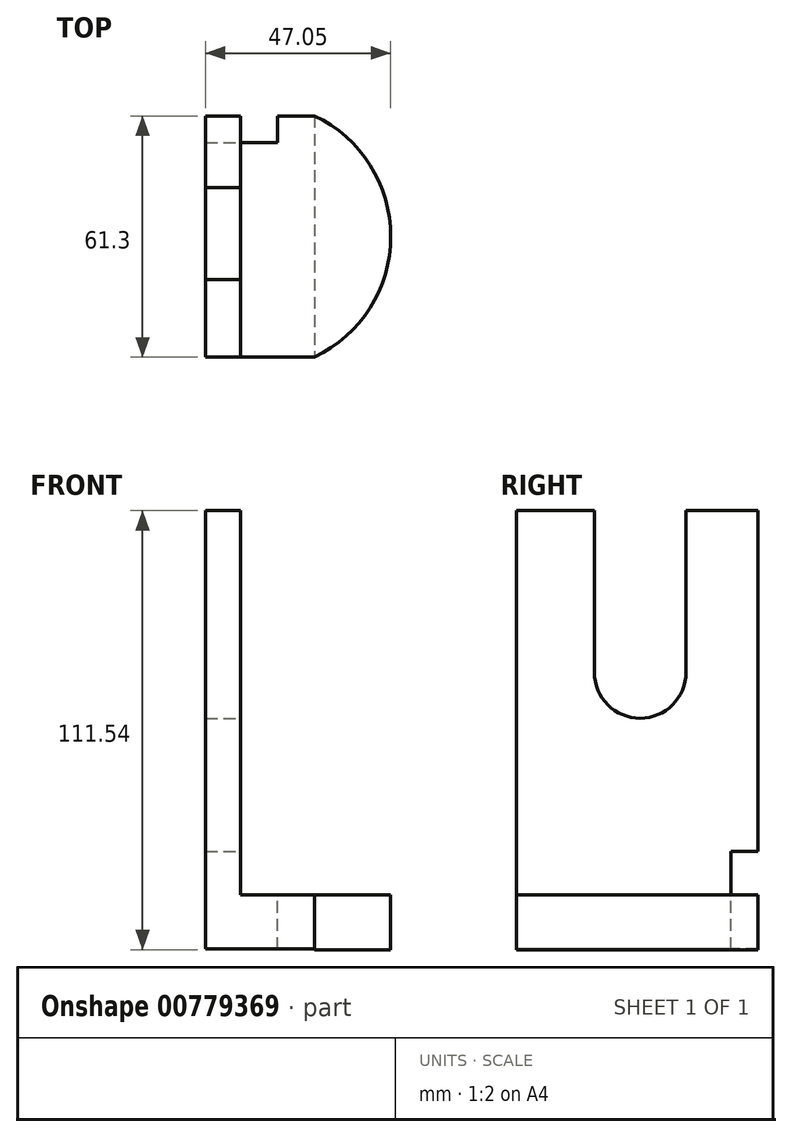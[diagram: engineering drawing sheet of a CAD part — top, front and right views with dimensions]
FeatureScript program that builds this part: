
annotation { "Feature Type Name" : "Feature", "Feature Type Description" : "" }
export const myFeature = defineFeature(function(context is Context, id is Id, definition is map)
    precondition{}
    {
        {
            var Q0;
            Q0=qCreatedBy(makeId("Right.planeOp"),FACE);
            var sketch = newSketch(context, id + "F0", { "sketchPlane" : qUnion([Q0])});
            skLineSegment(sketch, "E0.bottom", {"start": v(30.65, 55.7) * mm, "end": v(-30.65, 55.7) * mm});
            skLineSegment(sketch, "E0.top", {"start": v(30.65, -55.7) * mm, "end": v(-30.65, -55.7) * mm});
            skLineSegment(sketch, "E0.left", {"start": v(30.65, 55.7) * mm, "end": v(30.65, -55.7) * mm});
            skLineSegment(sketch, "E0.right", {"start": v(-30.65, 55.7) * mm, "end": v(-30.65, -55.7) * mm});
            skPoint(sketch, "E0.middle", {"position": v(0, 0) * mm});
            skSolve(sketch);
        }
        {
            var Q0;
            Q0=makeQuery(id+"F0.imprint","IMPRINT",FACE,{"disambiguationData":[TD([[makeQuery(id+"F0.imprint","IMPRINT",EDGE,{"derivedFrom":sQuery(id+"F0.wireOp",EDGE,"E0.bottom")}),1.0]])]});
            extrude(context, id + "F1", {"entities" : qUnion([Q0]), "depth" : 8.9 * mm, "offsetDistance" : 25.4 * mm});
        }
        {
            var Q0;
            Q0=makeQuery(id+"F1.opExtrude","CAP_FACE",FACE,{"disambiguationData":[OSD([sQuery(id+"F0.wireOp",EDGE,"E0.bottom"),sQuery(id+"F0.wireOp",EDGE,"E0.top"),sQuery(id+"F0.wireOp",EDGE,"E0.left"),sQuery(id+"F0.wireOp",EDGE,"E0.right")])],"isStart":false});
            var sketch = newSketch(context, id + "F2", { "sketchPlane" : qUnion([Q0])});
            skLineSegment(sketch, "E1", {"start": v(-30.65, -41.88) * mm, "end": v(30.65, -41.88) * mm});
            skLineSegment(sketch, "E2", {"start": v(30.65, -41.88) * mm, "end": v(30.65, -55.7) * mm});
            skLineSegment(sketch, "E3", {"start": v(30.65, -55.7) * mm, "end": v(-30.65, -55.7) * mm});
            skLineSegment(sketch, "E4", {"start": v(-30.65, -55.7) * mm, "end": v(-30.65, -41.88) * mm});
            skSolve(sketch);
        }
        {
            var Q0;
            Q0=makeQuery(id+"F2.imprint","IMPRINT",FACE,{"disambiguationData":[TD([[makeQuery(id+"F2.imprint","IMPRINT",EDGE,{"derivedFrom":sQuery(id+"F2.wireOp",EDGE,"E1")}),-1.0]])]});
            extrude(context, id + "F3", {"entities" : qUnion([Q0]), "operationType" : NewBodyOperationType.ADD, "depth" : 18.8 * mm, "offsetDistance" : 25.4 * mm});
        }
        {
            var Q0;
            Q0=makeQuery(id+"F3.opExtrude","SWEPT_FACE",FACE,{"disambiguationData":[OSD([sQuery(id+"F2.wireOp",EDGE,"E1")])]});
            var sketch = newSketch(context, id + "F4", { "sketchPlane" : qUnion([Q0])});
            skArc(sketch, "E5", {"start": v(27.69, -30.65) * mm, "mid": v(47.05, 0) * mm, "end": v(27.69, 30.65) * mm});
            skSolve(sketch);
        }
        {
            var Q0;
            Q0 = qSketchRegion(id + "F4", true);
            var Q1;
            Q1=makeQuery(id+"F4.imprint","IMPRINT",FACE,{"disambiguationData":[TD([[makeQuery(id+"F4.imprint","IMPRINT",EDGE,{"derivedFrom":sQuery(id+"F4.wireOp",EDGE,"E5")}),1.0]])]});
            extrude(context, id + "F5", {"entities" : qUnion([Q0, Q1]), "operationType" : NewBodyOperationType.ADD, "oppositeDirection" : true, "depth" : 13.97 * mm, "offsetDistance" : 25.4 * mm});
        }
        {
            var Q0;
            Q0=makeQuery(id+"F1.opExtrude","CAP_FACE",FACE,{"disambiguationData":[OSD([sQuery(id+"F0.wireOp",EDGE,"E0.bottom"),sQuery(id+"F0.wireOp",EDGE,"E0.top"),sQuery(id+"F0.wireOp",EDGE,"E0.left"),sQuery(id+"F0.wireOp",EDGE,"E0.right")])],"isStart":false});
            var sketch = newSketch(context, id + "F6", { "sketchPlane" : qUnion([Q0])});
            skLineSegment(sketch, "E6.bottom", {"start": v(-10.91, 55.7) * mm, "end": v(12.38, 55.7) * mm});
            skLineSegment(sketch, "E6.top", {"start": v(-10.91, 14.58) * mm, "end": v(12.38, 14.58) * mm});
            skLineSegment(sketch, "E6.left", {"start": v(-10.91, 55.7) * mm, "end": v(-10.91, 14.58) * mm});
            skLineSegment(sketch, "E6.right", {"start": v(12.38, 55.7) * mm, "end": v(12.38, 14.58) * mm});
            skSolve(sketch);
        }
        {
            var Q0;
            Q0 = qSketchRegion(id + "F6", true);
            var Q1;
            Q1=makeQuery(id+"F6.imprint","IMPRINT",FACE,{"disambiguationData":[TD([[makeQuery(id+"F6.imprint","IMPRINT",EDGE,{"derivedFrom":sQuery(id+"F6.wireOp",EDGE,"E6.bottom")}),1.0]])]});
            extrude(context, id + "F7", {"entities" : qUnion([Q0, Q1]), "operationType" : NewBodyOperationType.REMOVE, "oppositeDirection" : true, "depth" : 25.4 * mm, "offsetDistance" : 25.4 * mm});
        }
        {
            var Q0;
            Q0=makeQuery(id+"F1.opExtrude","CAP_FACE",FACE,{"disambiguationData":[OSD([sQuery(id+"F0.wireOp",EDGE,"E0.bottom"),sQuery(id+"F0.wireOp",EDGE,"E0.top"),sQuery(id+"F0.wireOp",EDGE,"E0.left"),sQuery(id+"F0.wireOp",EDGE,"E0.right")])],"isStart":false});
            var sketch = newSketch(context, id + "F8", { "sketchPlane" : qUnion([Q0])});
            skArc(sketch, "E7", {"start": v(-10.91, 14.58) * mm, "mid": v(0.73, 2.94) * mm, "end": v(12.38, 14.58) * mm});
            skSolve(sketch);
        }
        {
            var Q0;
            Q0=makeQuery(id+"F8.imprint","IMPRINT",FACE,{"disambiguationData":[TD([[makeQuery(id+"F8.imprint","IMPRINT",EDGE,{"derivedFrom":sQuery(id+"F8.wireOp",EDGE,"E7")}),1.0]])]});
            extrude(context, id + "F9", {"entities" : qUnion([Q0]), "operationType" : NewBodyOperationType.REMOVE, "oppositeDirection" : true, "depth" : 25.4 * mm, "offsetDistance" : 25.4 * mm});
        }
        {
            var Q0;
            Q0=makeQuery(id+"F1.opExtrude","CAP_FACE",FACE,{"disambiguationData":[OSD([sQuery(id+"F0.wireOp",EDGE,"E0.bottom"),sQuery(id+"F0.wireOp",EDGE,"E0.top"),sQuery(id+"F0.wireOp",EDGE,"E0.left"),sQuery(id+"F0.wireOp",EDGE,"E0.right")])],"isStart":false});
            var sketch = newSketch(context, id + "F10", { "sketchPlane" : qUnion([Q0])});
            skLineSegment(sketch, "E8.bottom", {"start": v(23.81, -41.88) * mm, "end": v(30.65, -41.88) * mm});
            skLineSegment(sketch, "E8.top", {"start": v(23.81, -30.92) * mm, "end": v(30.65, -30.92) * mm});
            skLineSegment(sketch, "E8.left", {"start": v(23.81, -41.88) * mm, "end": v(23.81, -30.92) * mm});
            skLineSegment(sketch, "E8.right", {"start": v(30.65, -41.88) * mm, "end": v(30.65, -30.92) * mm});
            skSolve(sketch);
        }
        {
            var Q0;
            Q0=makeQuery(id+"F10.imprint","IMPRINT",FACE,{"disambiguationData":[TD([[makeQuery(id+"F10.imprint","IMPRINT",EDGE,{"derivedFrom":sQuery(id+"F10.wireOp",EDGE,"E8.bottom")}),1.0]])]});
            extrude(context, id + "F11", {"entities" : qUnion([Q0]), "operationType" : NewBodyOperationType.REMOVE, "oppositeDirection" : true, "depth" : 25.4 * mm, "offsetDistance" : 25.4 * mm});
        }
        {
            var Q0;
            {var subQ0=sQuery(id+"F2.wireOp",EDGE,"E1");Q0=makeQuery(id+"F11.boolean.opBoolean","MERGE",FACE,{"derivedFrom":[makeQuery(id+"F5.boolean.opBoolean","MERGE",FACE,{"derivedFrom":[makeQuery(id+"F3.opExtrude","SWEPT_FACE",FACE,{"disambiguationData":[OSD([subQ0])]}),makeQuery(id+"F5.opExtrude","CAP_FACE",FACE,{"disambiguationData":[OSD([subQ0,sQuery(id+"F4.wireOp",EDGE,"E5")])],"isStart":true})]}),makeQuery(id+"F11.opExtrude","SWEPT_FACE",FACE,{"disambiguationData":[OSD([sQuery(id+"F10.wireOp",EDGE,"E8.bottom")])]})]});}
            var sketch = newSketch(context, id + "F12", { "sketchPlane" : qUnion([Q0])});
            skLineSegment(sketch, "E9.bottom", {"start": v(8.9, 23.81) * mm, "end": v(0, 23.81) * mm});
            skLineSegment(sketch, "E9.top", {"start": v(8.9, 30.65) * mm, "end": v(0, 30.65) * mm});
            skLineSegment(sketch, "E9.left", {"start": v(8.9, 23.81) * mm, "end": v(8.9, 30.65) * mm});
            skLineSegment(sketch, "E9.right", {"start": v(0, 23.81) * mm, "end": v(0, 30.65) * mm});
            skSolve(sketch);
        }
        {
            var Q0;
            Q0=makeQuery(id+"F12.imprint","IMPRINT",FACE,{"disambiguationData":[TD([[makeQuery(id+"F12.imprint","IMPRINT",EDGE,{"derivedFrom":sQuery(id+"F12.wireOp",EDGE,"E9.bottom")}),1.0]])]});
            extrude(context, id + "F13", {"entities" : qUnion([Q0]), "operationType" : NewBodyOperationType.REMOVE, "oppositeDirection" : true, "depth" : 25.4 * mm, "offsetDistance" : 25.4 * mm});
        }
        {
            var Q0;
            {var subQ0=sQuery(id+"F2.wireOp",EDGE,"E1");Q0=makeQuery(id+"F11.boolean.opBoolean","MERGE",FACE,{"derivedFrom":[makeQuery(id+"F5.boolean.opBoolean","MERGE",FACE,{"derivedFrom":[makeQuery(id+"F3.opExtrude","SWEPT_FACE",FACE,{"disambiguationData":[OSD([subQ0])]}),makeQuery(id+"F5.opExtrude","CAP_FACE",FACE,{"disambiguationData":[OSD([subQ0,sQuery(id+"F4.wireOp",EDGE,"E5")])],"isStart":true})]}),makeQuery(id+"F11.opExtrude","SWEPT_FACE",FACE,{"disambiguationData":[OSD([sQuery(id+"F10.wireOp",EDGE,"E8.bottom")])]})]});}
            var sketch = newSketch(context, id + "F14", { "sketchPlane" : qUnion([Q0])});
            skLineSegment(sketch, "E10.bottom", {"start": v(8.9, 23.81) * mm, "end": v(18.29, 23.81) * mm});
            skLineSegment(sketch, "E10.top", {"start": v(8.9, 30.65) * mm, "end": v(18.29, 30.65) * mm});
            skLineSegment(sketch, "E10.left", {"start": v(8.9, 23.81) * mm, "end": v(8.9, 30.65) * mm});
            skLineSegment(sketch, "E10.right", {"start": v(18.29, 23.81) * mm, "end": v(18.29, 30.65) * mm});
            skSolve(sketch);
        }
        {
            var Q0;
            Q0=makeQuery(id+"F14.imprint","IMPRINT",FACE,{"disambiguationData":[TD([[makeQuery(id+"F14.imprint","IMPRINT",EDGE,{"derivedFrom":sQuery(id+"F14.wireOp",EDGE,"E10.bottom")}),1.0]])]});
            extrude(context, id + "F15", {"entities" : qUnion([Q0]), "operationType" : NewBodyOperationType.REMOVE, "oppositeDirection" : true, "depth" : 25.4 * mm, "offsetDistance" : 25.4 * mm});
        }
    });
